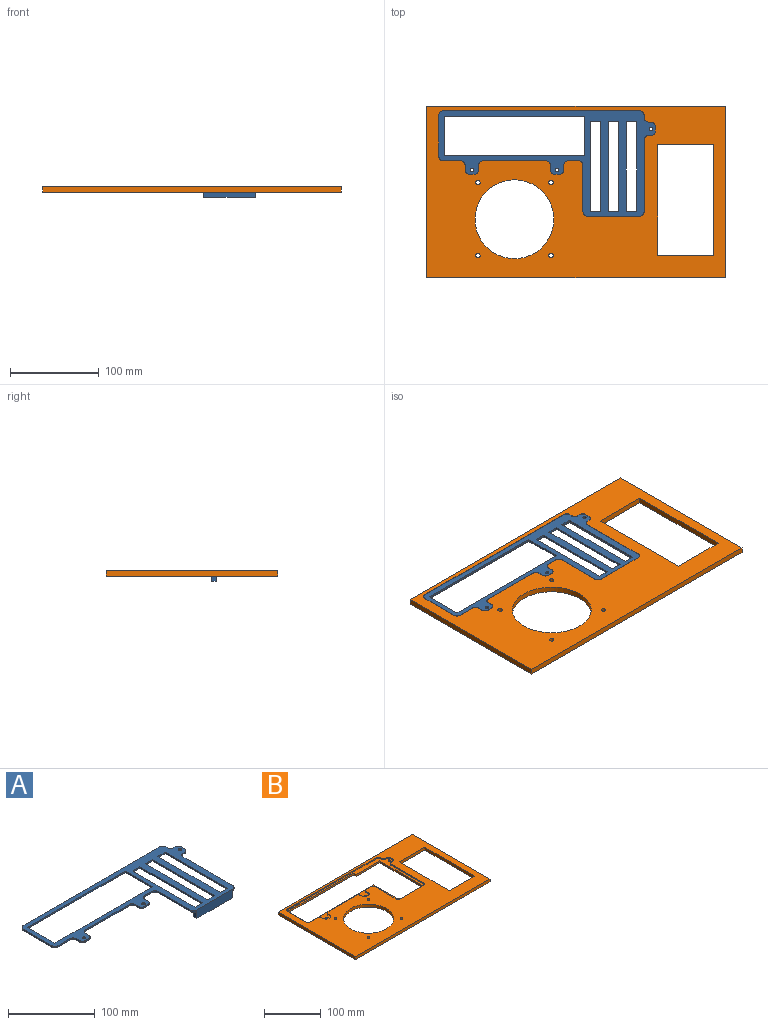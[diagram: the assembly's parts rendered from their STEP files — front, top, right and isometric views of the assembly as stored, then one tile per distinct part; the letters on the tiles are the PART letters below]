
ASSEMBLY  parts=2 mates=1
PART A: 58 faces, bbox 244.5x119x12 mm
  f0: plane 244.45x119mm, normal (0,0,-1), area 6968.8mm2, adj f1,f2,f3,f4,f5,f6,f7,f8
  f1: plane 158.75x2mm, normal (0,1,0), area 317.5mm2, adj f0,f2,f53,f54
  f2: plane 44.45x2mm, normal (1,0,0), area 88.9mm2, adj f0,f1,f3,f54
  f3: plane 158.75x2mm, normal (0,-1,0), area 317.5mm2, adj f0,f2,f53,f54
  f4: plane 101.6x2mm, normal (1,0,0), area 203.2mm2, adj f0,f5,f8,f54
  f5: plane 12x2mm, normal (0,-1,0), area 24mm2, adj f0,f4,f49,f54
  f6: plane 101.6x2mm, normal (1,0,0), area 203.2mm2, adj f0,f7,f8,f54
  f7: plane 12x2mm, normal (0,-1,0), area 24mm2, adj f0,f6,f50,f54
  f8: plane 58.08x12mm, normal (0,1,0), area 652.8mm2, adj f0,f4,f6,f9,f49,f50,f51,f54
  f9: plane 101.6x2mm, normal (1,0,0), area 203.2mm2, adj f0,f8,f10,f54
  f10: plane 12x2mm, normal (0,-1,0), area 24mm2, adj f0,f9,f51,f54
  f11: cylinder r=5.08mm len=5.08mm, axis (0,0,-1), area 16mm2, adj f0,f12,f52,f54
  f12: plane 58.84x12mm, normal (0,-1,0), area 698.5mm2, adj f0,f11,f13,f54,f55,f56,f57
  f13: cylinder r=5.08mm len=5.08mm, axis (0,0,-1), area 16mm2, adj f0,f12,f14,f54
  f14: plane 80.9x2mm, normal (1,0,0), area 161.8mm2, adj f0,f13,f15,f54
  f15: cylinder r=5.08mm len=5.08mm, axis (0,0,-1), area 16mm2, adj f0,f14,f16,f54
  f16: plane 2.54x2mm, normal (0,-1,0), area 5.1mm2, adj f0,f15,f17,f54
  f17: cylinder r=5.08mm len=5.08mm, axis (0,0,-1), area 16mm2, adj f0,f16,f18,f54
  f18: plane 5.08x2mm, normal (1,0,0), area 10.2mm2, adj f0,f17,f19,f54
  f19: cylinder r=5.08mm len=5.08mm, axis (0,0,-1), area 16mm2, adj f0,f18,f20,f54
  f20: plane 2.54x2mm, normal (0,1,0), area 5.1mm2, adj f0,f19,f21,f54
  f21: cylinder r=5.08mm len=5.08mm, axis (0,0,-1), area 16mm2, adj f0,f20,f22,f54
  f22: plane 2.54x2mm, normal (1,0,0), area 5.1mm2, adj f0,f21,f23,f54
  f23: cylinder r=5.08mm len=5.08mm, axis (0,0,-1), area 16mm2, adj f0,f22,f24,f54
  f24: plane 221.59x2mm, normal (0,1,0), area 443.2mm2, adj f0,f23,f25,f54
  f25: cylinder r=5.08mm len=5.08mm, axis (0,0,-1), area 16mm2, adj f0,f24,f26,f54
  f26: plane 46.29x2mm, normal (-1,0,0), area 92.6mm2, adj f0,f25,f27,f54
  f27: cylinder r=5.08mm len=5.08mm, axis (0,0,-1), area 16mm2, adj f0,f26,f28,f54
  f28: plane 19.5x2mm, normal (0,-1,0), area 39mm2, adj f0,f27,f29,f54
  f29: cylinder r=5.08mm len=5.08mm, axis (0,0,-1), area 16mm2, adj f0,f28,f30,f54
  f30: plane 5.08x2mm, normal (-1,0,0), area 10.2mm2, adj f0,f29,f31,f54
  f31: cylinder r=5.08mm len=5.08mm, axis (0,0,-1), area 16mm2, adj f0,f30,f32,f54
  f32: plane 5.08x2mm, normal (0,-1,0), area 10.2mm2, adj f0,f31,f33,f54
  f33: cylinder r=5.08mm len=5.08mm, axis (0,0,-1), area 16mm2, adj f0,f32,f34,f54
  f34: plane 5.08x2mm, normal (1,0,0), area 10.2mm2, adj f0,f33,f35,f54
  f35: cylinder r=5.08mm len=5.08mm, axis (0,0,-1), area 16mm2, adj f0,f34,f36,f54
  f36: plane 70.8x2mm, normal (0,-1,0), area 141.6mm2, adj f0,f35,f37,f54
  f37: cylinder r=5.08mm len=5.08mm, axis (0,0,-1), area 16mm2, adj f0,f36,f38,f54
  f38: plane 5.08x2mm, normal (-1,0,0), area 10.2mm2, adj f0,f37,f39,f54
  f39: cylinder r=5.08mm len=5.08mm, axis (0,0,-1), area 16mm2, adj f0,f38,f40,f54
  f40: plane 5.08x2mm, normal (0,-1,0), area 10.2mm2, adj f0,f39,f41,f54
  f41: cylinder r=5.08mm len=5.08mm, axis (0,0,-1), area 16mm2, adj f0,f40,f42,f54
  f42: plane 5.08x2mm, normal (1,0,0), area 10.2mm2, adj f0,f41,f43,f54
  f43: cylinder r=5.08mm len=5.08mm, axis (0,0,-1), area 16mm2, adj f0,f42,f44,f54
  f44: plane 11.5x2mm, normal (0,-1,0), area 23mm2, adj f0,f43,f45,f54
  f45: cylinder r=5.08mm len=5.08mm, axis (0,0,-1), area 16mm2, adj f0,f44,f52,f54
  f46: cylinder r=2mm len=4mm, axis (0,0,-1), area 25.1mm2, adj f0,f54
  f47: cylinder r=2mm len=4mm, axis (0,0,-1), area 25.1mm2, adj f0,f54
  f48: cylinder r=2mm len=4mm, axis (0,0,-1), area 25.1mm2, adj f0,f54
  f49: plane 101.6x2mm, normal (-1,0,0), area 203.2mm2, adj f0,f5,f8,f54
  f50: plane 101.6x2mm, normal (-1,0,0), area 203.2mm2, adj f0,f7,f8,f54
  f51: plane 101.6x2mm, normal (-1,0,0), area 203.2mm2, adj f0,f8,f10,f54
  f52: plane 52.39x2mm, normal (-1,0,0), area 104.8mm2, adj f0,f11,f45,f54
  f53: plane 44.45x2mm, normal (-1,0,0), area 88.9mm2, adj f0,f1,f3,f54
  f54: plane 244.45x119mm, normal (0,0,1), area 7282.4mm2, adj f1,f2,f3,f4,f5,f6,f7,f8
  f55: plane 10x5.4mm, normal (-1,0,0), area 54mm2, adj f0,f8,f12,f57
  f56: plane 10x5.4mm, normal (1,0,0), area 54mm2, adj f0,f8,f12,f57
  f57: plane 58.08x5.4mm, normal (0,0,-1), area 313.6mm2, adj f8,f12,f55,f56
PART B: 66 faces, bbox 336.6x193.7x6.4 mm
  f0: plane 5.4x4mm, normal (1,0,0), area 21.6mm2, adj f1,f21,f29,f65
  f1: plane 4x0.46mm, normal (0,1,0), area 1.8mm2, adj f0,f2,f29,f65
  f2: plane 60.15x4mm, normal (1,0,0), area 240.6mm2, adj f1,f3,f29,f65
  f3: plane 164.75x4mm, normal (0,1,0), area 659mm2, adj f2,f4,f29,f65
  f4: plane 50.45x4mm, normal (1,0,0), area 201.8mm2, adj f3,f5,f29,f65
  f5: plane 164.75x4mm, normal (0,-1,0), area 659mm2, adj f4,f6,f29,f65
  f6: plane 6x4mm, normal (-1,0,0), area 24mm2, adj f5,f7,f29,f65
  f7: plane 59x4mm, normal (0,-1,0), area 236mm2, adj f6,f8,f29,f65
  f8: plane 104.6x4mm, normal (-1,0,0), area 418.4mm2, adj f7,f9,f29,f65
  f9: plane 4x0.46mm, normal (0,1,0), area 1.8mm2, adj f8,f10,f29,f65
  f10: plane 5.4x4mm, normal (-1,0,0), area 21.6mm2, adj f9,f21,f29,f65
  f11: cylinder r=2mm len=4mm, axis (0,0,-1), area 50.3mm2, adj f29,f65
  f12: cylinder r=2mm len=4mm, axis (0,0,-1), area 50.3mm2, adj f29,f65
  f13: cylinder r=2mm len=4mm, axis (0,0,-1), area 50.3mm2, adj f29,f65
  f14: plane 336.55x193.65mm, normal (0,0,1), area 32902.1mm2, adj f15,f16,f17,f18,f19,f20,f21,f22
  f15: plane 125x6.4mm, normal (-1,0,0), area 800mm2, adj f14,f16,f22,f29
  f16: plane 63.5x6.4mm, normal (0,1,0), area 406.4mm2, adj f14,f15,f17,f29
  f17: plane 125x6.4mm, normal (1,0,0), area 800mm2, adj f14,f16,f22,f29
  f18: plane 193.65x6.4mm, normal (-1,0,0), area 1239.4mm2, adj f14,f19,f23,f29
  f19: plane 336.55x6.4mm, normal (0,-1,0), area 2153.9mm2, adj f14,f18,f20,f29
  f20: plane 193.65x6.4mm, normal (1,0,0), area 1239.4mm2, adj f14,f19,f23,f29
  f21: plane 58.84x6.4mm, normal (0,1,0), area 373.5mm2, adj f0,f10,f14,f29,f30,f64,f65
  f22: plane 63.5x6.4mm, normal (0,-1,0), area 406.4mm2, adj f14,f15,f17,f29
  f23: plane 336.55x6.4mm, normal (0,1,0), area 2153.9mm2, adj f14,f18,f20,f29
  f24: cylinder r=44.5mm len=89mm, axis (0,0,-1), area 1789.5mm2, adj f14,f29
  f25: cylinder r=2.5mm len=6.4mm, axis (0,0,-1), area 100.5mm2, adj f14,f29
  f26: cylinder r=2.5mm len=6.4mm, axis (0,0,-1), area 100.5mm2, adj f14,f29
  f27: cylinder r=2.5mm len=6.4mm, axis (0,0,-1), area 100.5mm2, adj f14,f29
  f28: cylinder r=2.5mm len=6.4mm, axis (0,0,-1), area 100.5mm2, adj f14,f29
  f29: plane 336.55x193.65mm, normal (0,0,-1), area 36101.4mm2, adj f0,f1,f2,f3,f4,f5,f6,f7
  f30: cylinder r=5.08mm len=5.08mm, axis (0,0,-1), area 19.2mm2, adj f14,f21,f31,f65
  f31: plane 80.9x2.4mm, normal (-1,0,0), area 194.2mm2, adj f14,f30,f32,f65
  f32: cylinder r=5.08mm len=5.08mm, axis (0,0,-1), area 19.2mm2, adj f14,f31,f33,f65
  f33: plane 2.54x2.4mm, normal (0,1,0), area 6.1mm2, adj f14,f32,f34,f65
  f34: cylinder r=5.08mm len=5.08mm, axis (0,0,-1), area 19.2mm2, adj f14,f33,f35,f65
  f35: plane 5.08x2.4mm, normal (-1,0,0), area 12.2mm2, adj f14,f34,f36,f65
  f36: cylinder r=5.08mm len=5.08mm, axis (0,0,-1), area 19.2mm2, adj f14,f35,f37,f65
  f37: plane 2.54x2.4mm, normal (0,-1,0), area 6.1mm2, adj f14,f36,f38,f65
  f38: cylinder r=5.08mm len=5.08mm, axis (0,0,-1), area 19.2mm2, adj f14,f37,f39,f65
  f39: plane 2.54x2.4mm, normal (-1,0,0), area 6.1mm2, adj f14,f38,f40,f65
  f40: cylinder r=5.08mm len=5.08mm, axis (0,0,-1), area 19.2mm2, adj f14,f39,f41,f65
  f41: plane 221.59x2.4mm, normal (0,-1,0), area 531.8mm2, adj f14,f40,f42,f65
  f42: cylinder r=5.08mm len=5.08mm, axis (0,0,-1), area 19.2mm2, adj f14,f41,f43,f65
  f43: plane 46.27x2.4mm, normal (1,0,0), area 111.1mm2, adj f14,f42,f44,f65
  f44: cylinder r=5.08mm len=5.08mm, axis (0,0,-1), area 19.2mm2, adj f14,f43,f45,f65
  f45: plane 19.5x2.4mm, normal (0,1,0), area 46.8mm2, adj f14,f44,f46,f65
  f46: cylinder r=5.08mm len=5.08mm, axis (0,0,-1), area 19.2mm2, adj f14,f45,f47,f65
  f47: plane 5.1x2.4mm, normal (1,0,0), area 12.2mm2, adj f14,f46,f48,f65
  f48: cylinder r=5.08mm len=5.08mm, axis (0,0,-1), area 19.2mm2, adj f14,f47,f49,f65
  f49: plane 5.08x2.4mm, normal (0,1,0), area 12.2mm2, adj f14,f48,f50,f65
  f50: cylinder r=5.08mm len=5.08mm, axis (0,0,-1), area 19.2mm2, adj f14,f49,f51,f65
  f51: plane 5.08x2.4mm, normal (-1,0,0), area 12.2mm2, adj f14,f50,f52,f65
  f52: cylinder r=5.08mm len=5.08mm, axis (0,0,-1), area 19.2mm2, adj f14,f51,f53,f65
  f53: plane 70.8x2.4mm, normal (0,1,0), area 169.9mm2, adj f14,f52,f54,f65
  f54: cylinder r=5.08mm len=5.08mm, axis (0,0,-1), area 19.2mm2, adj f14,f53,f55,f65
  f55: plane 5.08x2.4mm, normal (1,0,0), area 12.2mm2, adj f14,f54,f56,f65
  f56: cylinder r=5.08mm len=5.08mm, axis (0,0,-1), area 19.2mm2, adj f14,f55,f57,f65
  f57: plane 5.08x2.4mm, normal (0,1,0), area 12.2mm2, adj f14,f56,f58,f65
  f58: cylinder r=5.08mm len=5.08mm, axis (0,0,-1), area 19.2mm2, adj f14,f57,f59,f65
  f59: plane 5.08x2.4mm, normal (-1,0,0), area 12.2mm2, adj f14,f58,f60,f65
  f60: cylinder r=5.08mm len=5.08mm, axis (0,0,-1), area 19.2mm2, adj f14,f59,f61,f65
  f61: plane 11.5x2.4mm, normal (0,1,0), area 27.6mm2, adj f14,f60,f62,f65
  f62: cylinder r=5.08mm len=5.08mm, axis (0,0,-1), area 19.2mm2, adj f14,f61,f63,f65
  f63: plane 52.39x2.4mm, normal (1,0,0), area 125.7mm2, adj f14,f62,f64,f65
  f64: cylinder r=5.08mm len=5.08mm, axis (0,0,-1), area 19.2mm2, adj f14,f21,f63,f65
  f65: plane 244.45x119mm, normal (0,0,1), area 3199.2mm2, adj f0,f1,f2,f3,f4,f5,f6,f7
PLACE A t=(-448.43,1082.42,149.11)mm
PLACE B t=(-448.43,1245.11,145.11)mm
MATE fastened A.f46 <-> B.f13  axis (0,0,-1) through (-626.35,155.01,149.11)mm
